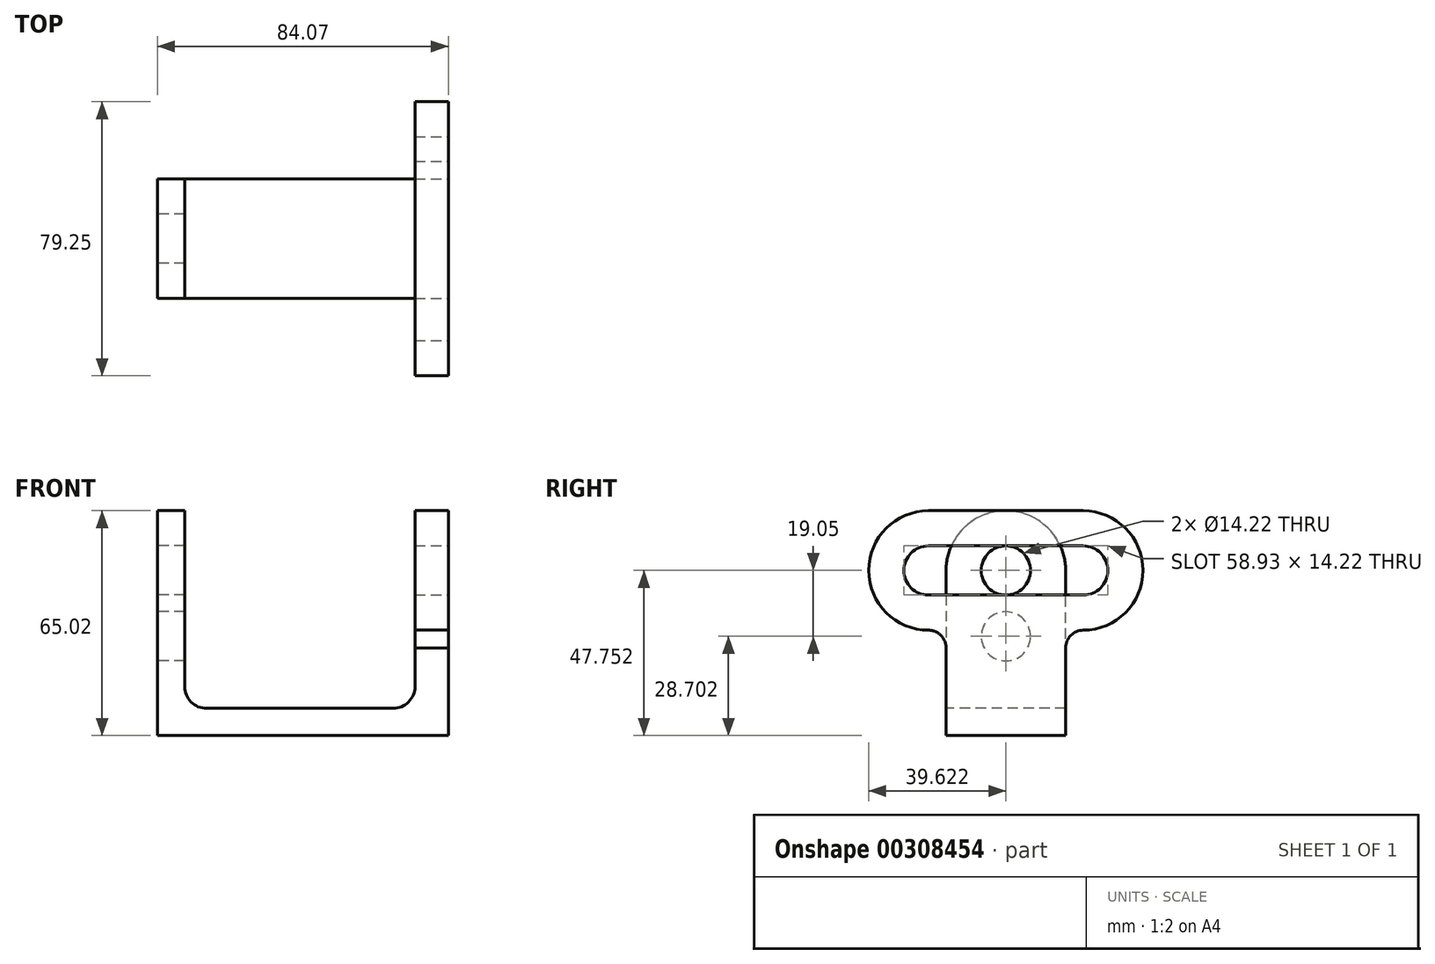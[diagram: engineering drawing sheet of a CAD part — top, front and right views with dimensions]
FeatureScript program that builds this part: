
annotation { "Feature Type Name" : "Feature", "Feature Type Description" : "" }
export const myFeature = defineFeature(function(context is Context, id is Id, definition is map)
    precondition{}
    {
        {
            var Q0;
            Q0=qCreatedBy(makeId("Front.planeOp"),FACE);
            var sketch = newSketch(context, id + "F0", { "sketchPlane" : qUnion([Q0])});
            skLineSegment(sketch, "E0", {"start": v(0, 0) * mm, "end": v(84.07, 0) * mm});
            skLineSegment(sketch, "E1", {"start": v(84.07, 0) * mm, "end": v(84.07, 7.87) * mm});
            skLineSegment(sketch, "E2", {"start": v(84.07, 7.87) * mm, "end": v(0, 7.87) * mm});
            skLineSegment(sketch, "E3", {"start": v(0, 7.87) * mm, "end": v(0, 0) * mm});
            skSolve(sketch);
        }
        {
            var Q0;
            Q0=makeQuery(id+"F0.imprint","IMPRINT",FACE,{"disambiguationData":[TD([[makeQuery(id+"F0.imprint","IMPRINT",EDGE,{"derivedFrom":sQuery(id+"F0.wireOp",EDGE,"E0")}),1.0]])]});
            extrude(context, id + "F1", {"entities" : qUnion([Q0]), "oppositeDirection" : true, "depth" : 34.54 * mm});
        }
        {
            var Q0;
            Q0=makeQuery(id+"F1.opExtrude","SWEPT_FACE",FACE,{"disambiguationData":[OSD([sQuery(id+"F0.wireOp",EDGE,"E1")])]});
            var sketch = newSketch(context, id + "F2", { "sketchPlane" : qUnion([Q0])});
            skLineSegment(sketch, "E4", {"start": v(0, 0) * mm, "end": v(17.27, 0) * mm, "construction": true});
            skLineSegment(sketch, "E5", {"start": v(17.27, 0) * mm, "end": v(17.27, 47.75) * mm, "construction": true});
            skLineSegment(sketch, "E6", {"start": v(17.27, 47.75) * mm, "end": v(39.62, 47.75) * mm, "construction": true});
            skLineSegment(sketch, "E7", {"start": v(17.27, 47.75) * mm, "end": v(-5.08, 47.75) * mm, "construction": true});
            skArc(sketch, "E8", {"start": v(39.62, 40.64) * mm, "mid": v(46.74, 47.75) * mm, "end": v(39.62, 54.86) * mm});
            skArc(sketch, "E9", {"start": v(-5.08, 54.86) * mm, "mid": v(-12.2, 47.75) * mm, "end": v(-5.08, 40.64) * mm});
            skLineSegment(sketch, "E10", {"start": v(-5.08, 54.86) * mm, "end": v(39.62, 54.86) * mm});
            skLineSegment(sketch, "E11", {"start": v(39.62, 40.64) * mm, "end": v(-5.08, 40.64) * mm});
            skArc(sketch, "E12", {"start": v(39.62, 65.02) * mm, "mid": v(56.9, 47.75) * mm, "end": v(39.62, 30.48) * mm});
            skArc(sketch, "E13", {"start": v(-5.08, 30.48) * mm, "mid": v(-22.35, 47.75) * mm, "end": v(-5.08, 65.02) * mm});
            skLineSegment(sketch, "E14", {"start": v(-5.08, 65.02) * mm, "end": v(39.62, 65.02) * mm});
            skArc(sketch, "E15", {"start": v(-5.08, 30.48) * mm, "mid": v(-1.47, 28.97) * mm, "end": v(0, 25.34) * mm});
            skLineSegment(sketch, "E16", {"start": v(0, 7.87) * mm, "end": v(0, 25.34) * mm});
            skLineSegment(sketch, "E17", {"start": v(34.54, 7.87) * mm, "end": v(34.54, 25.34) * mm});
            skArc(sketch, "E18", {"start": v(34.54, 25.34) * mm, "mid": v(36.03, 28.96) * mm, "end": v(39.62, 30.48) * mm});
            skSolve(sketch);
        }
        {
            var Q0;
            Q0=makeQuery(id+"F2.imprint","IMPRINT",FACE,{"disambiguationData":[TD([[makeQuery(id+"F2.imprint","IMPRINT",EDGE,{"derivedFrom":sQuery(id+"F2.wireOp",EDGE,"E8")}),-1.0]])]});
            extrude(context, id + "F3", {"entities" : qUnion([Q0]), "operationType" : NewBodyOperationType.ADD, "oppositeDirection" : true, "depth" : 9.65 * mm});
        }
        {
            var Q0;
            Q0=makeQuery(id+"F1.opExtrude","SWEPT_FACE",FACE,{"disambiguationData":[OSD([sQuery(id+"F0.wireOp",EDGE,"E3")])]});
            var sketch = newSketch(context, id + "F4", { "sketchPlane" : qUnion([Q0])});
            skLineSegment(sketch, "E19", {"start": v(-34.54, 0) * mm, "end": v(-34.54, 47.75) * mm});
            skLineSegment(sketch, "E20", {"start": v(-34.54, 47.75) * mm, "end": v(0, 47.75) * mm, "construction": true});
            skLineSegment(sketch, "E21", {"start": v(0, 47.75) * mm, "end": v(0, 0) * mm});
            skCircle(sketch, "E22", {"center": v(-17.27, 47.75) * mm, "radius": 7.11 * mm});
            skLineSegment(sketch, "E23", {"start": v(-17.27, 47.75) * mm, "end": v(-17.27, 28.7) * mm, "construction": true});
            skCircle(sketch, "E24", {"center": v(-17.27, 28.7) * mm, "radius": 7.11 * mm});
            skArc(sketch, "E25", {"start": v(0, 47.75) * mm, "mid": v(-17.27, 65.02) * mm, "end": v(-34.54, 47.75) * mm});
            skSolve(sketch);
        }
        {
            var Q0;
            Q0=makeQuery(id+"F4.imprint","IMPRINT",FACE,{"disambiguationData":[TD([[makeQuery(id+"F4.imprint","IMPRINT",EDGE,{"derivedFrom":sQuery(id+"F4.wireOp",EDGE,"E22")}),-1.0]])]});
            extrude(context, id + "F5", {"entities" : qUnion([Q0]), "operationType" : NewBodyOperationType.ADD, "oppositeDirection" : true, "depth" : 7.87 * mm});
        }
        {
            var Q0;
            Q0=makeQuery(id+"F5.boolean.opBoolean","MERGE",FACE,{"derivedFrom":[makeQuery(id+"F3.boolean.opBoolean","MERGE",FACE,{"derivedFrom":[makeQuery(id+"F1.opExtrude","CAP_FACE",FACE,{"disambiguationData":[OSD([sQuery(id+"F0.wireOp",EDGE,"E0"),sQuery(id+"F0.wireOp",EDGE,"E1"),sQuery(id+"F0.wireOp",EDGE,"E2"),sQuery(id+"F0.wireOp",EDGE,"E3")])],"isStart":true}),makeQuery(id+"F3.opExtrude","SWEPT_FACE",FACE,{"disambiguationData":[OSD([sQuery(id+"F2.wireOp",EDGE,"E16")])]})]}),makeQuery(id+"F5.opExtrude","SWEPT_FACE",FACE,{"disambiguationData":[OSD([sQuery(id+"F4.wireOp",EDGE,"E21")])]})]});
            var sketch = newSketch(context, id + "F6", { "sketchPlane" : qUnion([Q0])});
            skLineSegment(sketch, "E26", {"start": v(7.87, 7.87) * mm, "end": v(7.87, 14.22) * mm});
            skLineSegment(sketch, "E27", {"start": v(7.87, 7.87) * mm, "end": v(14.22, 7.87) * mm});
            skLineSegment(sketch, "E28", {"start": v(74.42, 7.87) * mm, "end": v(68.07, 7.87) * mm});
            skLineSegment(sketch, "E29", {"start": v(74.42, 7.87) * mm, "end": v(74.42, 14.22) * mm});
            skArc(sketch, "E30", {"start": v(7.87, 14.22) * mm, "mid": v(9.73, 9.73) * mm, "end": v(14.22, 7.87) * mm});
            skArc(sketch, "E31", {"start": v(68.07, 7.87) * mm, "mid": v(72.56, 9.73) * mm, "end": v(74.42, 14.22) * mm});
            skSolve(sketch);
        }
        {
            var Q0;
            Q0=makeQuery(id+"F6.imprint","IMPRINT",FACE,{"disambiguationData":[TD([[makeQuery(id+"F6.imprint","IMPRINT",EDGE,{"derivedFrom":sQuery(id+"F6.wireOp",EDGE,"E28")}),-1.0]])]});
            var Q1;
            Q1=makeQuery(id+"F6.imprint","IMPRINT",FACE,{"disambiguationData":[TD([[makeQuery(id+"F6.imprint","IMPRINT",EDGE,{"derivedFrom":sQuery(id+"F6.wireOp",EDGE,"E26")}),1.0]])]});
            extrude(context, id + "F7", {"entities" : qUnion([Q0, Q1]), "operationType" : NewBodyOperationType.ADD, "oppositeDirection" : true, "depth" : 34.54 * mm});
        }
    });
